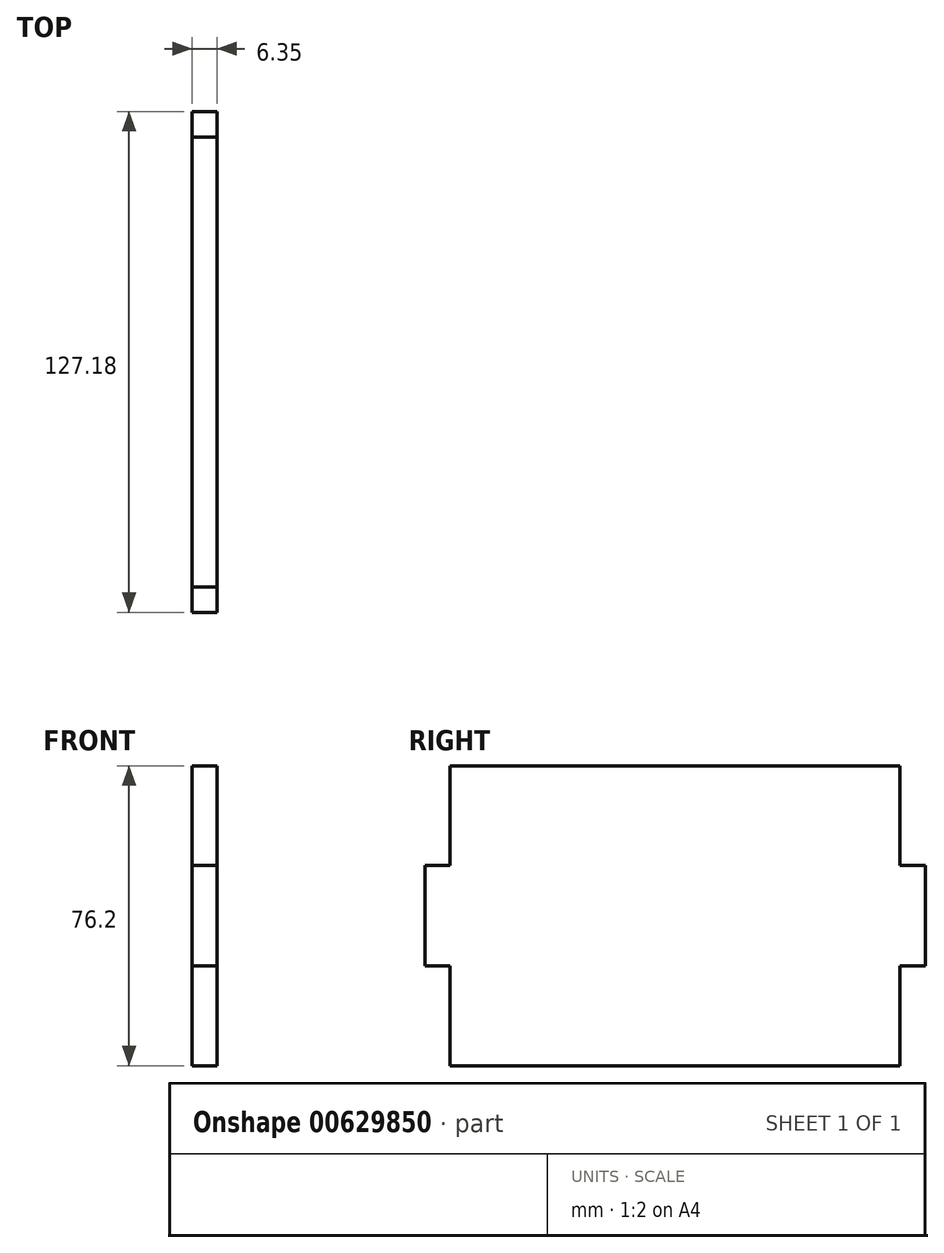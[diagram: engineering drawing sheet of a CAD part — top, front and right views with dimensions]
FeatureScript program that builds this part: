
annotation { "Feature Type Name" : "Feature", "Feature Type Description" : "" }
export const myFeature = defineFeature(function(context is Context, id is Id, definition is map)
    precondition{}
    {
        {
            var Q0;
            Q0=qCreatedBy(makeId("Right.planeOp"),FACE);
            var sketch = newSketch(context, id + "F0", { "sketchPlane" : qUnion([Q0])});
            skLineSegment(sketch, "E0.bottom", {"start": v(0, 0) * mm, "end": v(114.3, 0) * mm});
            skLineSegment(sketch, "E0.top", {"start": v(0, 76.2) * mm, "end": v(114.3, 76.2) * mm});
            skLineSegment(sketch, "E0.left", {"start": v(0, 0) * mm, "end": v(0, 76.2) * mm});
            skLineSegment(sketch, "E0.right", {"start": v(114.3, 0) * mm, "end": v(114.3, 76.2) * mm});
            skLineSegment(sketch, "E1.bottom", {"start": v(18.96, 0) * mm, "end": v(44.54, 0) * mm});
            skLineSegment(sketch, "E1.top", {"start": v(18.96, -6.44) * mm, "end": v(44.54, -6.44) * mm});
            skLineSegment(sketch, "E1.left", {"start": v(18.96, 0) * mm, "end": v(18.96, -6.44) * mm});
            skLineSegment(sketch, "E1.right", {"start": v(44.54, 0) * mm, "end": v(44.54, -6.44) * mm});
            skLineSegment(sketch, "E2.bottom", {"start": v(69.76, 0) * mm, "end": v(95.34, 0) * mm});
            skLineSegment(sketch, "E2.top", {"start": v(69.76, -6.44) * mm, "end": v(95.34, -6.44) * mm});
            skLineSegment(sketch, "E2.left", {"start": v(69.76, 0) * mm, "end": v(69.76, -6.44) * mm});
            skLineSegment(sketch, "E2.right", {"start": v(95.34, 0) * mm, "end": v(95.34, -6.44) * mm});
            skLineSegment(sketch, "E3.bottom", {"start": v(-6.44, 50.89) * mm, "end": v(0, 50.89) * mm});
            skLineSegment(sketch, "E3.top", {"start": v(-6.44, 25.31) * mm, "end": v(0, 25.31) * mm});
            skLineSegment(sketch, "E3.left", {"start": v(-6.44, 50.89) * mm, "end": v(-6.44, 25.31) * mm});
            skLineSegment(sketch, "E3.right", {"start": v(0, 50.89) * mm, "end": v(0, 25.31) * mm});
            skLineSegment(sketch, "E4.bottom", {"start": v(114.3, 50.89) * mm, "end": v(120.74, 50.89) * mm});
            skLineSegment(sketch, "E4.top", {"start": v(114.3, 25.31) * mm, "end": v(120.74, 25.31) * mm});
            skLineSegment(sketch, "E4.left", {"start": v(114.3, 50.89) * mm, "end": v(114.3, 25.31) * mm});
            skLineSegment(sketch, "E4.right", {"start": v(120.74, 50.89) * mm, "end": v(120.74, 25.31) * mm});
            skPoint(sketch, "E5", {"position": v(-6.44, 38.1) * mm});
            skPoint(sketch, "E6", {"position": v(82.55, -6.44) * mm});
            skPoint(sketch, "E7", {"position": v(31.75, -6.44) * mm});
            skSolve(sketch);
        }
        {
            var Q0;
            {var subQ2=sQuery(id+"F0.wireOp",EDGE,"E0.top");Q0=makeQuery(id+"F0.imprint","IMPRINT",FACE,{"disambiguationData":[TD([[makeQuery(id+"F0.imprint","IMPRINT",EDGE,{"derivedFrom":subQ2}),-1.0]])]});}
            var Q1;
            Q1=makeQuery(id+"F0.imprint","IMPRINT",FACE,{"disambiguationData":[TD([[makeQuery(id+"F0.imprint","IMPRINT",EDGE,{"derivedFrom":sQuery(id+"F0.wireOp",EDGE,"E3.bottom")}),-1.0]])]});
            var Q2;
            Q2=makeQuery(id+"F0.imprint","IMPRINT",FACE,{"disambiguationData":[TD([[makeQuery(id+"F0.imprint","IMPRINT",EDGE,{"derivedFrom":sQuery(id+"F0.wireOp",EDGE,"E1.bottom")}),-1.0]])]});
            var Q3;
            Q3=makeQuery(id+"F0.imprint","IMPRINT",FACE,{"disambiguationData":[TD([[makeQuery(id+"F0.imprint","IMPRINT",EDGE,{"derivedFrom":sQuery(id+"F0.wireOp",EDGE,"E2.bottom")}),-1.0]])]});
            var Q4;
            Q4=makeQuery(id+"F0.imprint","IMPRINT",FACE,{"disambiguationData":[TD([[makeQuery(id+"F0.imprint","IMPRINT",EDGE,{"derivedFrom":sQuery(id+"F0.wireOp",EDGE,"E4.bottom")}),-1.0]])]});
            extrude(context, id + "F1", {"entities" : qUnion([Q0, Q1, Q2, Q3, Q4]), "depth" : 6.35 * mm, "offsetDistance" : 25.4 * mm});
        }
    });
